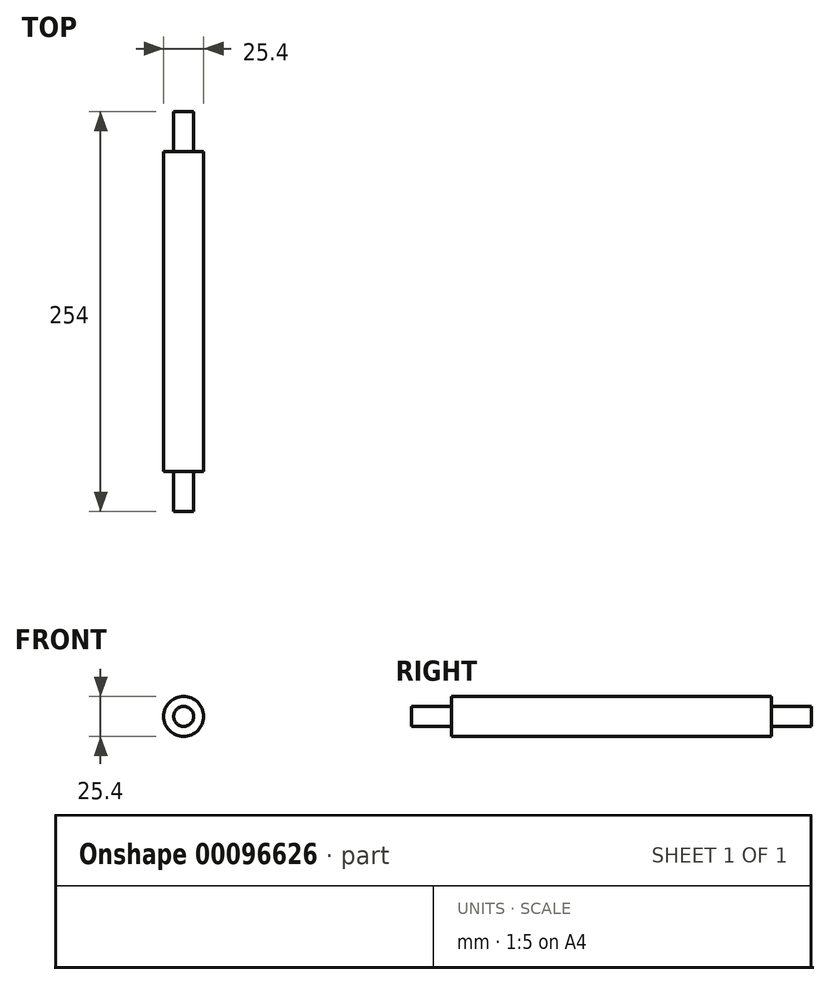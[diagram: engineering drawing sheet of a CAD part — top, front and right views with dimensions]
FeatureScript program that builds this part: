
annotation { "Feature Type Name" : "Feature", "Feature Type Description" : "" }
export const myFeature = defineFeature(function(context is Context, id is Id, definition is map)
    precondition{}
    {
        {
            var Q0;
            Q0=qCreatedBy(makeId("Front.planeOp"),FACE);
            var sketch = newSketch(context, id + "F0", { "sketchPlane" : qUnion([Q0])});
            skCircle(sketch, "E0", {"center": v(0, 0) * mm, "radius": 12.7 * mm});
            skSolve(sketch);
        }
        {
            var Q0;
            Q0=makeQuery(id+"F0.imprint","IMPRINT",FACE,{"disambiguationData":[TD([[makeQuery(id+"F0.imprint","IMPRINT",EDGE,{"derivedFrom":sQuery(id+"F0.wireOp",EDGE,"E0")}),1.0]])]});
            extrude(context, id + "F1", {"entities" : qUnion([Q0]), "depth" : 203.2 * mm});
        }
        {
            var Q0;
            Q0=makeQuery(id+"F1.opExtrude","CAP_FACE",FACE,{"disambiguationData":[OSD([sQuery(id+"F0.wireOp",EDGE,"E0")])],"isStart":false});
            var sketch = newSketch(context, id + "F2", { "sketchPlane" : qUnion([Q0])});
            skCircle(sketch, "E1", {"center": v(0, 0) * mm, "radius": 6.35 * mm});
            skSolve(sketch);
        }
        {
            var Q0;
            Q0=makeQuery(id+"F2.imprint","IMPRINT",FACE,{"disambiguationData":[TD([[makeQuery(id+"F2.imprint","IMPRINT",EDGE,{"derivedFrom":sQuery(id+"F2.wireOp",EDGE,"E1")}),1.0]])]});
            extrude(context, id + "F3", {"entities" : qUnion([Q0]), "operationType" : NewBodyOperationType.ADD, "depth" : 25.4 * mm});
        }
        {
            var Q0;
            Q0=makeQuery(id+"F1.opExtrude","CAP_FACE",FACE,{"disambiguationData":[OSD([sQuery(id+"F0.wireOp",EDGE,"E0")])],"isStart":true});
            var sketch = newSketch(context, id + "F4", { "sketchPlane" : qUnion([Q0])});
            skCircle(sketch, "E2", {"center": v(0, 0) * mm, "radius": 6.35 * mm});
            skSolve(sketch);
        }
        {
            var Q0;
            Q0 = qSketchRegion(id + "F4", true);
            extrude(context, id + "F5", {"entities" : qUnion([Q0]), "operationType" : NewBodyOperationType.ADD, "depth" : 25.4 * mm});
        }
    });
